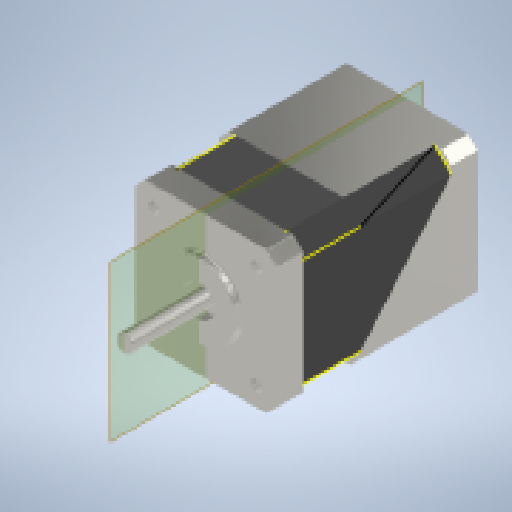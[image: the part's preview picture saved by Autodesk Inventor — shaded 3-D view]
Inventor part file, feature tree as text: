
AUTODESK INVENTOR PART (.ipt)
format: ipt  version: 2025 (Build 290162000, 162)  size: 692,224 bytes
history: native  units: mm
features: extrude x19, chamfer x12, fillet x7, sketch x6, thread x4, plane x1
ambient origin geometry x8: Origin, YZ Plane, XZ Plane, XY Plane, X Axis, Y Axis, Z Axis, Center Point
bodies: Solid1 (feature_tree)
feature tree (49):
  extrude  "Extrusion1"  Depth=42.0mm
  chamfer  "Chamfer6"  Distance=60.0mm
  chamfer  "Chamfer7"  Distance=3.0mm Angle=45.0deg
  chamfer  "Chamfer8"  Distance=3.0mm Angle=45.0deg
  chamfer  "Chamfer9"  Distance=3.0mm Angle=45.0deg
  chamfer  "Chamfer10"  Distance=35.0mm
  chamfer  "Chamfer11"  Distance=3.0mm Angle=45.0deg
  chamfer  "Chamfer12"  Distance=3.0mm Angle=45.0deg
  chamfer  "Chamfer13"  Distance=35.0mm
  chamfer  "Chamfer14"  Distance=5.0mm Angle=45.0deg
  chamfer  "Chamfer15"  Distance=16.989mm
  chamfer  "Chamfer16"  Distance=3.0mm Angle=45.0deg
  chamfer  "Chamfer17"  Distance=3.0mm Angle=45.0deg
  extrude  "Extrusion3"  Depth=3.0mm TaperAngle=45.0deg
  extrude  "Extrusion4"  Depth=0.01mm TaperAngle=0.0deg
  extrude  "Extrusion5"  Depth=0.01mm TaperAngle=0.0deg
  extrude  "Extrusion6"  Depth=0.01mm TaperAngle=0.0deg
  extrude  "Extrusion7"  Depth=0.01mm TaperAngle=0.0deg
  extrude  "Extrusion8"  Depth=22.0mm
  extrude  "Extrusion9"  Depth=2.0mm TaperAngle=0.0deg
  extrude  "Extrusion10"  Depth=9.5mm
  extrude  "Extrusion11"  Depth=3.0mm TaperAngle=0.0deg
  fillet  "Fillet1"  Radius=5.0mm
  extrude  "Extrusion12"  Depth=25.0mm TaperAngle=0.0deg
  thread  "Thread1"  [1 undecoded]
  thread  "Thread2"  [1 undecoded]
  thread  "Thread3"  [1 undecoded]
  thread  "Thread4"  [1 undecoded]
  extrude  "Extrusion13"  Depth=5.8mm
  extrude  "Extrusion14"  Depth=5.8mm
  extrude  "Extrusion15"  Depth=3.2mm
  fillet  "Fillet2"  Radius=5.8mm
  fillet  "Fillet3"  Radius=5.8mm
  extrude  "Extrusion16"  Depth=3.1mm
  extrude  "Extrusion17"  Depth=5.8mm
  extrude  "Extrusion18"  Depth=5.8mm
  extrude  "Extrusion19"  Depth=3.1mm
  extrude  "Extrusion20"  Depth=5.8mm
  fillet  "Fillet4"  Radius=5.8mm
  fillet  "Fillet5"  Radius=3.1mm
  fillet  "Fillet6"  Radius=50.0mm
  fillet  "Fillet8"  Radius=4.0mm
  plane  "Work Plane1"
  sketch  "Sketch10"  dims[d0=42.0mm d1=42.0mm d2=60.0mm d3=0.0mm]
  sketch  "Sketch23"  dims[d32=5.0mm d33=2.0mm d34=45.0deg d35=8.0mm d36=44.0mm d37=8.0mm d38=3.0mm d39=2.0mm d40=45.0deg d41=3.0mm d42=2.0mm d43=45.0deg d44=3.0mm d45=2.0mm d46=45.0deg d47=0.0mm d48=35.0mm d49=25.0mm]
  sketch  "Sketch27"  dims[d50=5.0mm d51=2.0mm d52=45.0deg d53=0.002mm d54=16.998mm d55=8.0mm d56=3.0mm d57=2.0mm d58=45.0deg d59=3.0mm d60=2.0mm d61=45.0deg d62=0.0mm d63=35.0mm d64=25.0mm d65=5.0mm d66=2.0mm d67=45.0deg d68=0.011mm d69=16.989mm d70=8.0mm d71=3.0mm d72=2.0mm d73=45.0deg d74=3.0mm d75=2.0mm d76=45.0deg]
  sketch  "Sketch32"  dims[d77=0.0mm d78=35.0mm d79=25.0mm]
  sketch  "Sketch35"  dims[d80=5.0mm d81=2.0mm d82=45.0deg d83=0.015mm d84=16.985mm d85=8.0mm d86=3.0mm d87=2.0mm d88=45.0deg]
  sketch  "Sketch36"  dims[d89=8.0mm d90=0.0mm d91=0.01mm d92=0.0mm d93=0.01mm d94=0.0mm d95=0.01mm d96=0.0mm d97=0.01mm d98=0.0mm d99=22.0mm d100=2.0mm d101=0.0mm d102=9.5mm d103=3.0mm d104=0.0mm d105=5.0mm d106=25.0mm d107=0.0mm d108=15.0mm d109=4.5mm d110=25.0mm d111=0.0mm d112=0.25mm d113=5.8mm d114=5.8mm d115=3.2mm d116=5.8mm d117=5.8mm d118=3.1mm d119=5.8mm d120=5.8mm d121=3.1mm d122=5.8mm d123=5.8mm d124=3.1mm d125=50.0mm d126=0.0mm d127=4.0mm d128=0.0mm d129=4.0mm d130=0.0mm d131=50.0mm d132=0.0mm d133=4.0mm d134=0.0mm d135=7.0mm d136=4.0mm d137=0.0mm d138=5.8mm d139=5.8mm d140=5.8mm d141=5.8mm d142=2.5mm d143=0.0mm d144=16.0mm d145=8.0mm d146=2.0mm d147=4.3mm d148=0.0mm d149=0.5mm d150=0.2mm d151=5.5mm d152=15.0mm d153=0.5mm d154=6.0mm d155=0.0mm d156=3.9mm d157=13.0mm d158=1.0mm d159=4.5mm d160=0.0mm d161=7.8mm d162=3.9mm d163=4.5mm d164=0.0mm d165=4.0mm d166=1.0mm d167=1.0mm d168=1.0mm d169=1.0mm d170=0.84mm d171=0.0mm d172=0.5mm d173=0.5mm d174=0.5mm d175=1.6mm d176=0.5mm d177=0.5mm d178=0.5mm d179=0.5mm d180=1.6mm d181=1.6mm d182=1.6mm d184=1.6mm d185=1.0mm d186=1.0mm d187=4.0mm d188=0.0mm d189=0.2mm d190=0.3mm d191=0.3mm d193=0.05mm d194=0.0mm d196=0.5mm d197=0.5mm d198=0.0mm d195=0.872665mm]
note: 4 required parameter values undecoded (feature->parameter linkage not recoverable at this tier; creation-order binding heuristic only, values carry confidence <= 0.55)
